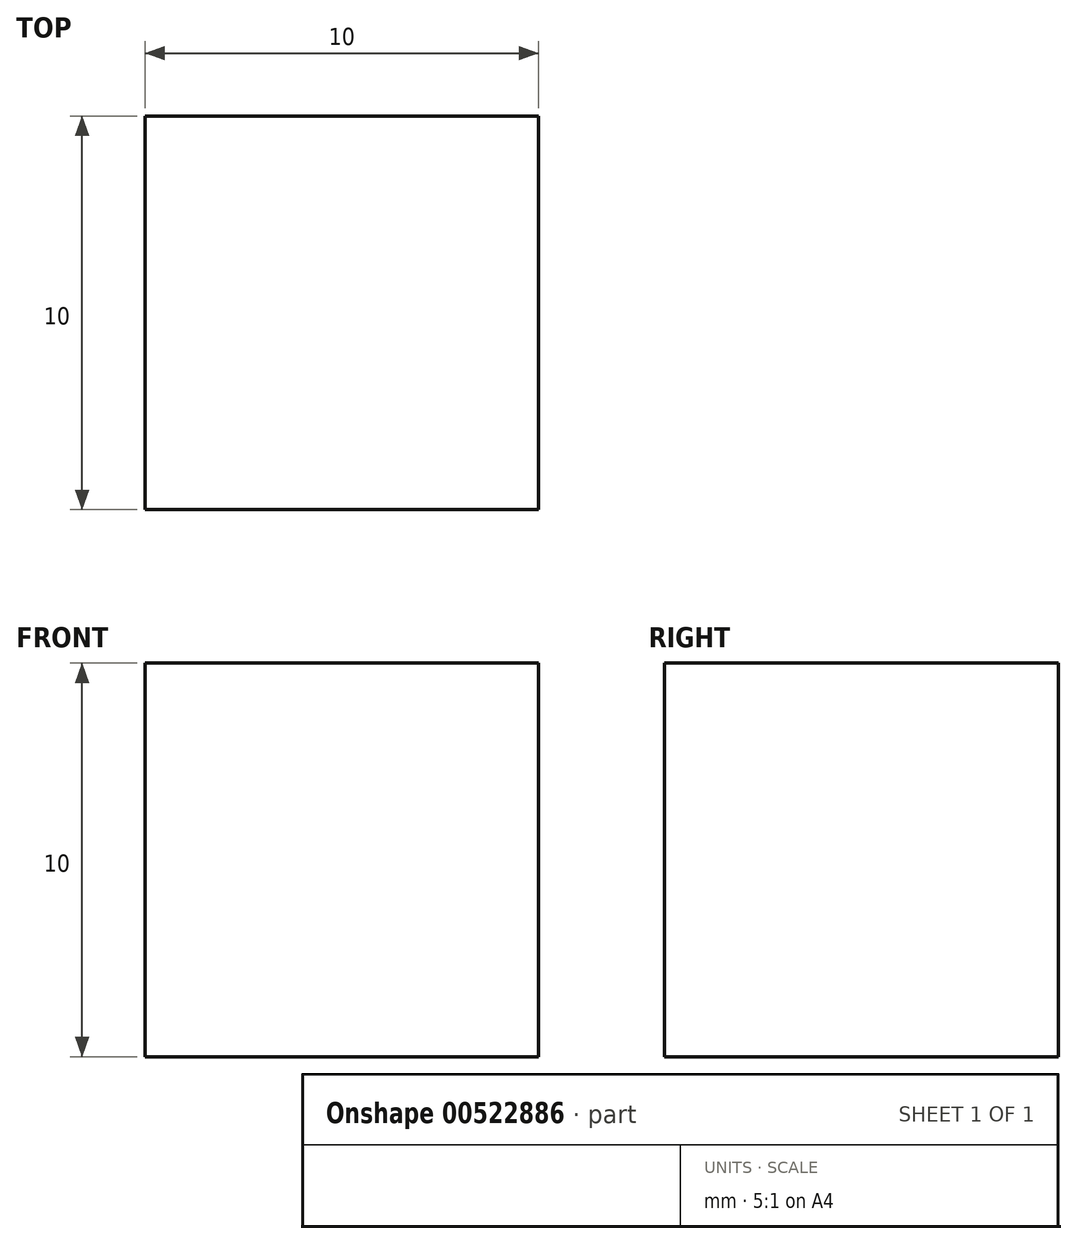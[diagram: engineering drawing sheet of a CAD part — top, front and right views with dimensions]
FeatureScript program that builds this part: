
annotation { "Feature Type Name" : "Feature", "Feature Type Description" : "" }
export const myFeature = defineFeature(function(context is Context, id is Id, definition is map)
    precondition{}
    {
        {
            var Q0;
            Q0=qCreatedBy(makeId("Top.planeOp"),FACE);
            var sketch = newSketch(context, id + "F0", { "sketchPlane" : qUnion([Q0])});
            skLineSegment(sketch, "E0.rect.bottom", {"start": v(-5, 5) * mm, "end": v(5, 5) * mm});
            skLineSegment(sketch, "E0.rect.top", {"start": v(-5, -5) * mm, "end": v(5, -5) * mm});
            skLineSegment(sketch, "E0.rect.left", {"start": v(-5, 5) * mm, "end": v(-5, -5) * mm});
            skLineSegment(sketch, "E0.rect.right", {"start": v(5, 5) * mm, "end": v(5, -5) * mm});
            skPoint(sketch, "E0.rect.middle", {"position": v(0, 0) * mm});
            skSolve(sketch);
        }
        {
            var Q0;
            Q0=qSketchRegion(id+"F0",true);
            extrude(context, id + "F1", {"entities" : qUnion([Q0]), "depth" : 10 * mm, "offsetDistance" : 25 * mm});
        }
    });
